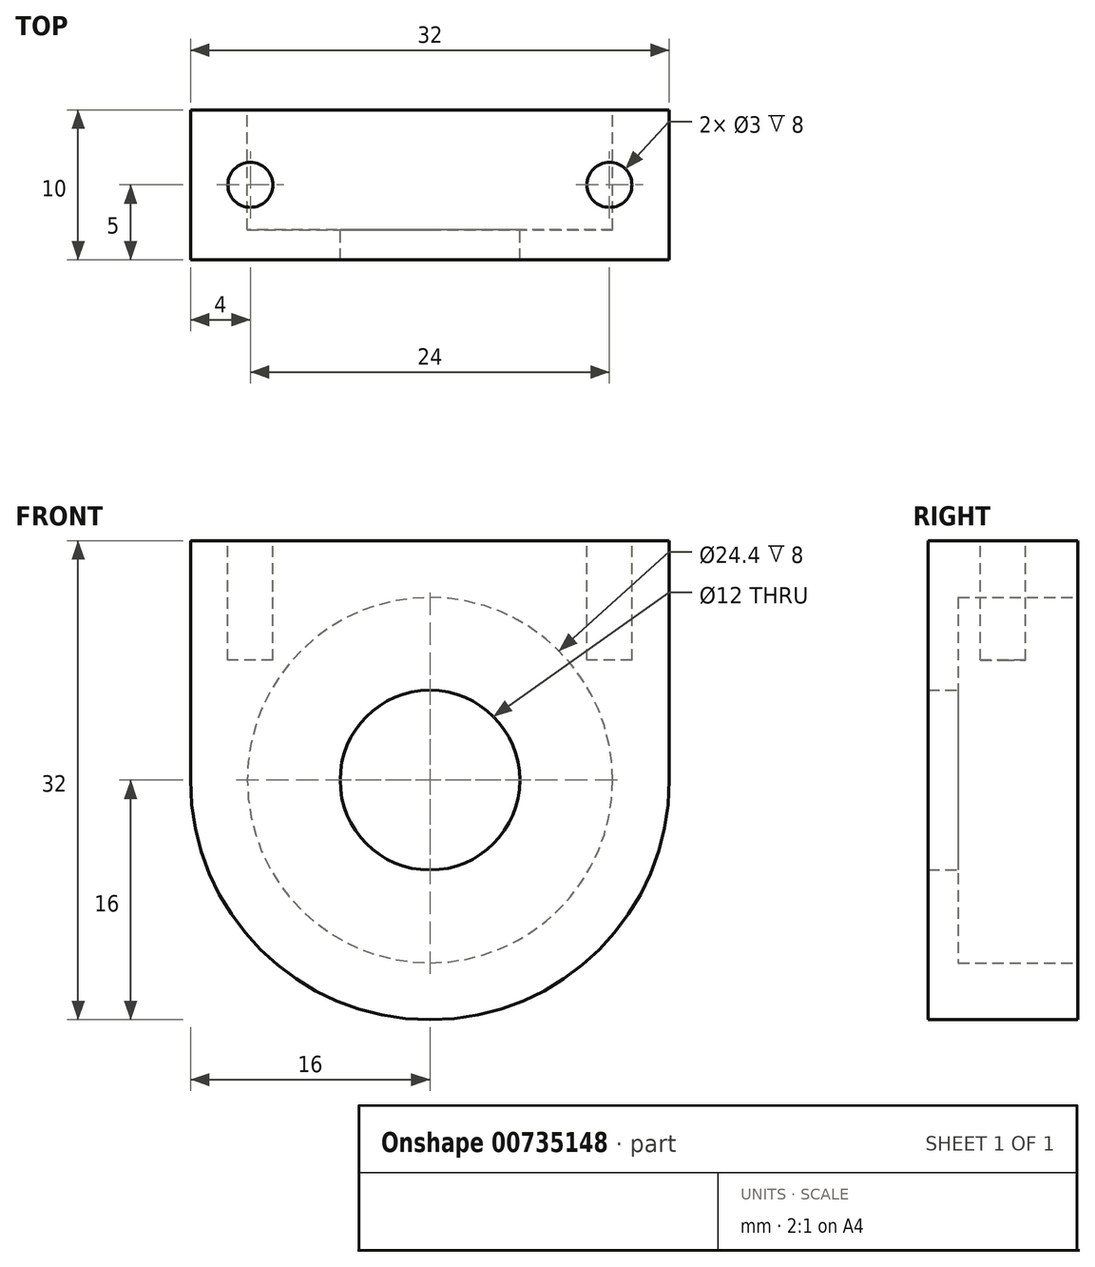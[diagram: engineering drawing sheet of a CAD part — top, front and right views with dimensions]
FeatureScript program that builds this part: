
annotation { "Feature Type Name" : "Feature", "Feature Type Description" : "" }
export const myFeature = defineFeature(function(context is Context, id is Id, definition is map)
    precondition{}
    {
        {
            var Q0;
            Q0=qCreatedBy(makeId("Front.planeOp"),FACE);
            var sketch = newSketch(context, id + "F0", { "sketchPlane" : qUnion([Q0])});
            skCircle(sketch, "E0", {"center": v(0, 0) * mm, "radius": 16 * mm});
            skLineSegment(sketch, "E1.bottom", {"start": v(-16, 0) * mm, "end": v(16, 0) * mm});
            skLineSegment(sketch, "E1.top", {"start": v(-16, 16) * mm, "end": v(16, 16) * mm});
            skLineSegment(sketch, "E1.left", {"start": v(-16, 0) * mm, "end": v(-16, 16) * mm});
            skLineSegment(sketch, "E1.right", {"start": v(16, 0) * mm, "end": v(16, 16) * mm});
            skSolve(sketch);
        }
        {
            var Q0;
            Q0 = qSketchRegion(id + "F0", true);
            extrude(context, id + "F1", {"entities" : qUnion([Q0]), "depth" : 10 * mm, "offsetDistance" : 25 * mm});
        }
        {
            var Q0;
            Q0=makeQuery(id+"F1.opExtrude","CAP_FACE",FACE,{"disambiguationData":[OSD([sQuery(id+"F0.wireOp",EDGE,"E0"),sQuery(id+"F0.wireOp",EDGE,"E1.top"),sQuery(id+"F0.wireOp",EDGE,"E1.left"),sQuery(id+"F0.wireOp",EDGE,"E1.right")])],"isStart":true});
            var sketch = newSketch(context, id + "F2", { "sketchPlane" : qUnion([Q0])});
            skCircle(sketch, "E2", {"center": v(0, 0) * mm, "radius": 12.2 * mm});
            skSolve(sketch);
        }
        {
            var Q0;
            Q0 = qSketchRegion(id + "F2", true);
            extrude(context, id + "F3", {"entities" : qUnion([Q0]), "operationType" : NewBodyOperationType.REMOVE, "oppositeDirection" : true, "depth" : 8 * mm, "offsetDistance" : 25 * mm});
        }
        {
            var Q0;
            Q0=makeQuery(id+"F3.boolean.opBoolean","COPY",FACE,{"derivedFrom":makeQuery(id+"F3.opExtrude","CAP_FACE",FACE,{"disambiguationData":[OSD([sQuery(id+"F2.wireOp",EDGE,"E2")])],"isStart":false})});
            var sketch = newSketch(context, id + "F4", { "sketchPlane" : qUnion([Q0])});
            skCircle(sketch, "E3", {"center": v(0, 0) * mm, "radius": 6 * mm});
            skSolve(sketch);
        }
        {
            var Q0;
            Q0=makeQuery(id+"F4.imprint","IMPRINT",FACE,{"disambiguationData":[TD([[makeQuery(id+"F4.imprint","IMPRINT",EDGE,{"derivedFrom":sQuery(id+"F4.wireOp",EDGE,"E3")}),1.0]])]});
            extrude(context, id + "F5", {"entities" : qUnion([Q0]), "operationType" : NewBodyOperationType.REMOVE, "oppositeDirection" : true, "depth" : 25 * mm, "offsetDistance" : 25 * mm});
        }
        {
            var Q0;
            Q0=makeQuery(id+"F1.opExtrude","SWEPT_FACE",FACE,{"disambiguationData":[OSD([sQuery(id+"F0.wireOp",EDGE,"E1.top")])]});
            var sketch = newSketch(context, id + "F6", { "sketchPlane" : qUnion([Q0])});
            skCircle(sketch, "E4", {"center": v(-12, -5) * mm, "radius": 1.5 * mm});
            skPoint(sketch, "E4.centerSnap0", {"position": v(-16, -5) * mm});
            skCircle(sketch, "E5", {"center": v(12, -5) * mm, "radius": 1.5 * mm});
            skPoint(sketch, "E5.centerSnap0", {"position": v(16, -5) * mm});
            skSolve(sketch);
        }
        {
            var Q0;
            Q0=makeQuery(id+"F6.imprint","IMPRINT",FACE,{"disambiguationData":[TD([[makeQuery(id+"F6.imprint","IMPRINT",EDGE,{"derivedFrom":sQuery(id+"F6.wireOp",EDGE,"E4")}),1.0]])]});
            var Q1;
            Q1=makeQuery(id+"F6.imprint","IMPRINT",FACE,{"disambiguationData":[TD([[makeQuery(id+"F6.imprint","IMPRINT",EDGE,{"derivedFrom":sQuery(id+"F6.wireOp",EDGE,"E5")}),1.0]])]});
            extrude(context, id + "F7", {"entities" : qUnion([Q0, Q1]), "operationType" : NewBodyOperationType.REMOVE, "oppositeDirection" : true, "depth" : 8 * mm, "offsetDistance" : 25 * mm});
        }
    });
